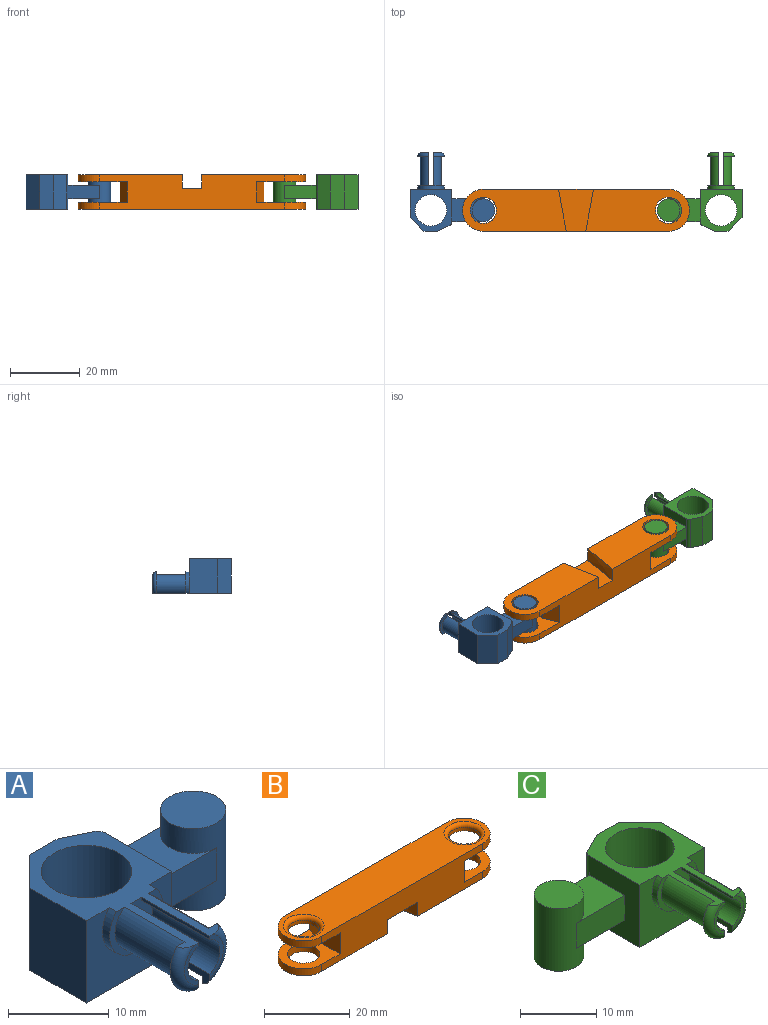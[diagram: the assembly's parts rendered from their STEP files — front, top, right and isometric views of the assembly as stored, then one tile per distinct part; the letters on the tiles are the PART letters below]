
ASSEMBLY  parts=3 mates=2
PART A: 33 faces, bbox 24.4x22.6x11.3 mm
  f0: plane 6.17x3mm, normal (0,1,0), area 5.5mm2, adj f3,f4,f27,f31
  f1: plane 9.5x0.38mm, normal (-1,0,0), area 3.6mm2, adj f2,f4,f5,f6
  f2: cylinder r=2.25mm len=9.5mm, axis (0,1,0), area 52.6mm2, adj f1,f3,f5,f6
  f3: plane 9.64x1.69mm, normal (-1,0,0), area 8mm2, adj f0,f2,f5,f6,f27,f31
  f4: plane 22.5x12mm, normal (0,0,1), area 92.8mm2, adj f0,f1,f5,f6,f7,f8,f10,f11
  f5: plane 5.15x2mm, normal (0,-1,0), area 3.1mm2, adj f1,f2,f3,f4,f31
  f6: plane 7.5x6.25mm, normal (0,-1,0), area 29.7mm2, adj f1,f2,f3,f4,f18,f21,f24,f25
  f7: plane 10x8mm, normal (-1,0,0), area 80mm2, adj f4,f9,f10,f19
  f8: plane 10x9.38mm, normal (1,0,0), area 67.8mm2, adj f4,f9,f14,f15,f16,f17,f19,f20
  f9: plane 12x12mm, normal (0,0,-1), area 68.3mm2, adj f7,f8,f10,f11,f12,f13,f19,f20
  f10: plane 10x4mm, normal (-0.71,0.71,0), area 56.6mm2, adj f4,f7,f9,f13
  f11: plane 10x3.45mm, normal (0.45,0.89,0), area 38.5mm2, adj f4,f9,f13,f20
  f12: cylinder r=4.5mm len=10mm, axis (0,0,-1), area 282.7mm2, adj f4,f9
  f13: plane 10x4mm, normal (0,1,0), area 40mm2, adj f4,f9,f10,f11
  f14: plane 9x4mm, normal (0,1,0), area 36mm2, adj f8,f16,f17,f28
  f15: plane 9x4mm, normal (0,-1,0), area 36mm2, adj f8,f16,f17,f28
  f16: plane 9x6.5mm, normal (0,0,1), area 41.9mm2, adj f8,f14,f15,f28
  f17: plane 9x6.5mm, normal (0,0,-1), area 41.9mm2, adj f8,f14,f15,f28
  f18: cylinder r=3.75mm len=7.5mm, axis (0,-1,0), area 17.3mm2, adj f4,f6,f19
  f19: plane 12x10mm, normal (0,-1,0), area 80.7mm2, adj f4,f7,f8,f9,f18
  f20: cylinder r=1mm len=10mm, axis (0,0,-1), area 11.1mm2, adj f4,f8,f9,f11
  f21: plane 9.64x1.69mm, normal (1,0,0), area 8mm2, adj f6,f22,f23,f24,f26,f32
  f22: plane 5.15x2mm, normal (0,-1,0), area 3.1mm2, adj f4,f21,f24,f25,f32
  f23: plane 6.17x3mm, normal (0,1,0), area 5.5mm2, adj f4,f21,f26,f32
  f24: cylinder r=2.25mm len=9.5mm, axis (0,1,0), area 52.6mm2, adj f6,f21,f22,f25
  f25: plane 9.5x0.38mm, normal (1,0,0), area 3.6mm2, adj f4,f6,f22,f24
  f26: cylinder r=3mm len=8.5mm, axis (0,1,0), area 58.7mm2, adj f4,f6,f21,f23
  f27: cylinder r=3mm len=8.5mm, axis (0,1,0), area 58.7mm2, adj f0,f3,f4,f6
  f28: cylinder r=3.25mm len=10mm, axis (0,0,-1), area 163.4mm2, adj f14,f15,f16,f17,f29,f30
  f29: plane 6.5x6.5mm, normal (0,0,1), area 33.2mm2, adj f28
  f30: plane 6.5x6.5mm, normal (0,0,-1), area 33.2mm2, adj f28
  f31: torus R=2.75mm, axis (0,-1,0), area 11.6mm2, adj f0,f3,f4,f5
  f32: torus R=2.75mm, axis (0,-1,0), area 11.6mm2, adj f4,f21,f22,f23
PART B: 26 faces, bbox 65x12.4x10 mm
  f0: plane 53x10mm, normal (0,1,0), area 411.5mm2, adj f1,f2,f5,f6,f7,f11,f12,f13
  f1: plane 30.08x12.39mm, normal (0,0,-1), area 282.6mm2, adj f0,f7,f8,f9,f21
  f2: cylinder r=6mm len=12mm, axis (0,0,-1), area 37.7mm2, adj f0,f8,f11,f16
  f3: cylinder r=3.75mm len=7.5mm, axis (0,0,-1), area 23.6mm2, adj f16,f25
  f4: cylinder r=3.75mm len=7.5mm, axis (0,0,-1), area 23.6mm2, adj f13,f24
  f5: cylinder r=6mm len=12mm, axis (0,0,-1), area 37.7mm2, adj f0,f8,f11,f13
  f6: cylinder r=6mm len=12mm, axis (0,0,-1), area 37.7mm2, adj f0,f8,f12,f14
  f7: cylinder r=6mm len=12mm, axis (0,0,-1), area 37.7mm2, adj f0,f1,f8,f17
  f8: plane 53x10mm, normal (0,-1,0), area 418mm2, adj f1,f2,f5,f6,f7,f11,f12,f13
  f9: cylinder r=3.75mm len=7.5mm, axis (0,0,-1), area 47.1mm2, adj f1,f17
  f10: cylinder r=3.75mm len=7.5mm, axis (0,0,-1), area 47.1mm2, adj f12,f14
  f11: plane 65x12mm, normal (0,0,1), area 607.3mm2, adj f0,f2,f5,f8,f24,f25
  f12: plane 30.08x12.39mm, normal (0,0,-1), area 282.6mm2, adj f0,f6,f8,f10,f22
  f13: plane 14x12mm, normal (0,0,-1), area 89.4mm2, adj f0,f4,f5,f8,f15,f19
  f14: plane 14x12mm, normal (0,0,1), area 89.4mm2, adj f0,f6,f8,f10,f15,f19
  f15: plane 7x6mm, normal (1,0,0), area 42mm2, adj f8,f13,f14,f19
  f16: plane 14x12mm, normal (0,0,-1), area 89.4mm2, adj f0,f2,f3,f8,f18,f20
  f17: plane 14x12mm, normal (0,0,1), area 89.4mm2, adj f0,f7,f8,f9,f18,f20
  f18: plane 7x6mm, normal (-1,0,0), area 42mm2, adj f8,f16,f17,f20
  f19: plane 6x5mm, normal (0.93,0.37,0), area 32.3mm2, adj f0,f13,f14,f15
  f20: plane 6x5mm, normal (-0.93,0.37,0), area 32.3mm2, adj f0,f16,f17,f18
  f21: extruded ~12x4mm, area 48.8mm2, adj f0,f1,f8,f23
  f22: extruded ~12x4mm, area 48.8mm2, adj f0,f8,f12,f23
  f23: plane 12.39x10mm, normal (0,0,-1), area 95.6mm2, adj f0,f8,f21,f22
  f24: torus R=4.75mm, axis (0,0,1), area 40.6mm2, adj f4,f11
  f25: torus R=4.75mm, axis (0,0,1), area 40.6mm2, adj f3,f11
PART C: 33 faces, bbox 24.4x22.6x11.3 mm
  f0: plane 6.17x3mm, normal (0,1,0), area 5.5mm2, adj f3,f4,f27,f31
  f1: plane 9.5x0.38mm, normal (1,0,0), area 3.6mm2, adj f2,f4,f5,f6
  f2: cylinder r=2.25mm len=9.5mm, axis (0,1,0), area 52.6mm2, adj f1,f3,f5,f6
  f3: plane 9.64x1.69mm, normal (1,0,0), area 8mm2, adj f0,f2,f5,f6,f27,f31
  f4: plane 22.5x12mm, normal (0,0,1), area 92.8mm2, adj f0,f1,f5,f6,f7,f8,f10,f11
  f5: plane 5.15x2mm, normal (0,-1,0), area 3.1mm2, adj f1,f2,f3,f4,f31
  f6: plane 7.5x6.25mm, normal (0,-1,0), area 29.7mm2, adj f1,f2,f3,f4,f18,f21,f24,f25
  f7: plane 10x8mm, normal (1,0,0), area 80mm2, adj f4,f9,f10,f19
  f8: plane 10x9.38mm, normal (-1,0,0), area 67.8mm2, adj f4,f9,f14,f15,f16,f17,f19,f20
  f9: plane 12x12mm, normal (0,0,-1), area 68.3mm2, adj f7,f8,f10,f11,f12,f13,f19,f20
  f10: plane 10x4mm, normal (0.71,0.71,0), area 56.6mm2, adj f4,f7,f9,f13
  f11: plane 10x3.45mm, normal (-0.45,0.89,0), area 38.5mm2, adj f4,f9,f13,f20
  f12: cylinder r=4.5mm len=10mm, axis (0,0,-1), area 282.7mm2, adj f4,f9
  f13: plane 10x4mm, normal (0,1,0), area 40mm2, adj f4,f9,f10,f11
  f14: plane 9x4mm, normal (0,1,0), area 36mm2, adj f8,f16,f17,f28
  f15: plane 9x4mm, normal (0,-1,0), area 36mm2, adj f8,f16,f17,f28
  f16: plane 9x6.5mm, normal (0,0,1), area 41.9mm2, adj f8,f14,f15,f28
  f17: plane 9x6.5mm, normal (0,0,-1), area 41.9mm2, adj f8,f14,f15,f28
  f18: cylinder r=3.75mm len=7.5mm, axis (0,-1,0), area 17.3mm2, adj f4,f6,f19
  f19: plane 12x10mm, normal (0,-1,0), area 80.7mm2, adj f4,f7,f8,f9,f18
  f20: cylinder r=1mm len=10mm, axis (0,0,-1), area 11.1mm2, adj f4,f8,f9,f11
  f21: plane 9.64x1.69mm, normal (-1,0,0), area 8mm2, adj f6,f22,f23,f24,f26,f32
  f22: plane 5.15x2mm, normal (0,-1,0), area 3.1mm2, adj f4,f21,f24,f25,f32
  f23: plane 6.17x3mm, normal (0,1,0), area 5.5mm2, adj f4,f21,f26,f32
  f24: cylinder r=2.25mm len=9.5mm, axis (0,1,0), area 52.6mm2, adj f6,f21,f22,f25
  f25: plane 9.5x0.38mm, normal (-1,0,0), area 3.6mm2, adj f4,f6,f22,f24
  f26: cylinder r=3mm len=8.5mm, axis (0,1,0), area 58.7mm2, adj f4,f6,f21,f23
  f27: cylinder r=3mm len=8.5mm, axis (0,1,0), area 58.7mm2, adj f0,f3,f4,f6
  f28: cylinder r=3.25mm len=10mm, axis (0,0,-1), area 163.4mm2, adj f14,f15,f16,f17,f29,f30
  f29: plane 6.5x6.5mm, normal (0,0,1), area 33.2mm2, adj f28
  f30: plane 6.5x6.5mm, normal (0,0,-1), area 33.2mm2, adj f28
  f31: torus R=2.75mm, axis (0,-1,0), area 11.6mm2, adj f0,f3,f4,f5
  f32: torus R=2.75mm, axis (0,-1,0), area 11.6mm2, adj f4,f21,f22,f23
PLACE A rot(axis=(-1,0,0),180deg) t=(-34.56,20.68,112.95)mm
PLACE B rot(axis=(-1,0,0),180deg) t=(50.64,-11.59,112.95)mm
PLACE C rot(axis=(-1,0,0),180deg) t=(90.49,20.68,112.95)mm
MATE fastened C.f28 <-> B.f4  axis (0,0,-1) through (54.46,31.19,102.95)mm
MATE fastened A.f28 <-> B.f2  axis (0,0,-1) through (1.46,31.19,102.95)mm
